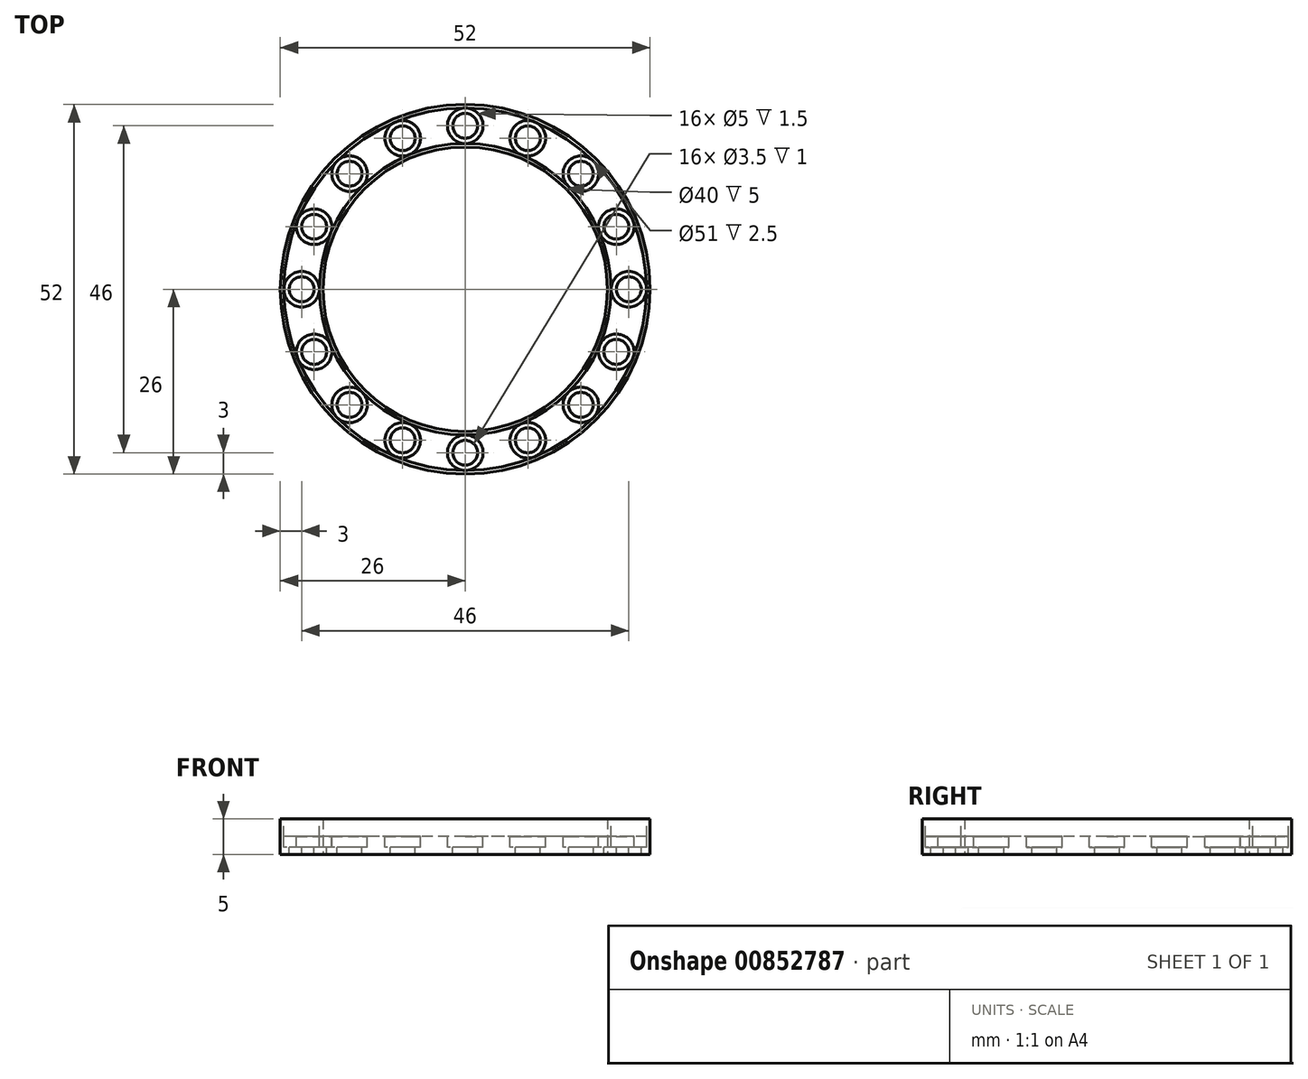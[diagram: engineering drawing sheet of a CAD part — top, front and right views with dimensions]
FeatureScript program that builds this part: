
annotation { "Feature Type Name" : "Feature", "Feature Type Description" : "" }
export const myFeature = defineFeature(function(context is Context, id is Id, definition is map)
    precondition{}
    {
        {
            var Q0;
            Q0=qCreatedBy(makeId("Top.planeOp"),FACE);
            var sketch = newSketch(context, id + "F0", { "sketchPlane" : qUnion([Q0])});
            skCircle(sketch, "E0", {"center": v(0, 0) * mm, "radius": 26 * mm});
            skCircle(sketch, "E1", {"center": v(0, 0) * mm, "radius": 20 * mm});
            skSolve(sketch);
        }
        {
            var Q0;
            Q0 = qSketchRegion(id + "F0", true);
            extrude(context, id + "F1", {"entities" : qUnion([Q0]), "depth" : 5 * mm, "offsetDistance" : 25 * mm});
        }
        {
            var Q0;
            Q0=makeQuery(id+"F1.opExtrude","CAP_FACE",FACE,{"disambiguationData":[OSD([sQuery(id+"F0.wireOp",EDGE,"E0"),sQuery(id+"F0.wireOp",EDGE,"E1")])],"isStart":false});
            var sketch = newSketch(context, id + "F2", { "sketchPlane" : qUnion([Q0])});
            skCircle(sketch, "E2", {"center": v(0, 0) * mm, "radius": 20.5 * mm});
            skCircle(sketch, "E3", {"center": v(0, 0) * mm, "radius": 25.5 * mm});
            skSolve(sketch);
        }
        {
            var Q0;
            Q0 = qSketchRegion(id + "F2", true);
            extrude(context, id + "F3", {"entities" : qUnion([Q0]), "operationType" : NewBodyOperationType.REMOVE, "oppositeDirection" : true, "depth" : 2.5 * mm, "offsetDistance" : 25 * mm});
        }
        {
            var Q0;
            Q0=makeQuery(id+"F3.boolean.opBoolean","COPY",FACE,{"derivedFrom":makeQuery(id+"F3.opExtrude","CAP_FACE",FACE,{"disambiguationData":[OSD([sQuery(id+"F2.wireOp",EDGE,"E2"),sQuery(id+"F2.wireOp",EDGE,"E3")])],"isStart":false})});
            var sketch = newSketch(context, id + "F4", { "sketchPlane" : qUnion([Q0])});
            skCircle(sketch, "E4", {"center": v(23, 0) * mm, "radius": 2.5 * mm});
            skCircle(sketch, "E5.1.0", {"center": v(21.25, -8.8) * mm, "radius": 2.5 * mm});
            skCircle(sketch, "E5.2.0", {"center": v(16.26, -16.26) * mm, "radius": 2.5 * mm});
            skCircle(sketch, "E5.3.0", {"center": v(8.8, -21.25) * mm, "radius": 2.5 * mm});
            skCircle(sketch, "E5.4.0", {"center": v(0, -23) * mm, "radius": 2.5 * mm});
            skCircle(sketch, "E5.5.0", {"center": v(-8.8, -21.25) * mm, "radius": 2.5 * mm});
            skCircle(sketch, "E5.6.0", {"center": v(-16.26, -16.26) * mm, "radius": 2.5 * mm});
            skCircle(sketch, "E5.7.0", {"center": v(-21.25, -8.8) * mm, "radius": 2.5 * mm});
            skCircle(sketch, "E5.8.0", {"center": v(-23, 0) * mm, "radius": 2.5 * mm});
            skCircle(sketch, "E5.9.0", {"center": v(-21.25, 8.8) * mm, "radius": 2.5 * mm});
            skCircle(sketch, "E5.10.0", {"center": v(-16.26, 16.26) * mm, "radius": 2.5 * mm});
            skCircle(sketch, "E5.11.0", {"center": v(-8.8, 21.25) * mm, "radius": 2.5 * mm});
            skCircle(sketch, "E5.12.0", {"center": v(0, 23) * mm, "radius": 2.5 * mm});
            skCircle(sketch, "E5.13.0", {"center": v(8.8, 21.25) * mm, "radius": 2.5 * mm});
            skCircle(sketch, "E5.14.0", {"center": v(16.26, 16.26) * mm, "radius": 2.5 * mm});
            skCircle(sketch, "E5.15.0", {"center": v(21.25, 8.8) * mm, "radius": 2.5 * mm});
            skPoint(sketch, "E5.center", {"position": v(0, 0) * mm});
            skLineSegment(sketch, "E5.anchor1", {"start": v(0, 0) * mm, "end": v(23, 0) * mm, "construction": true});
            skLineSegment(sketch, "E5.anchor2", {"start": v(0, 0) * mm, "end": v(21.25, 8.8) * mm, "construction": true});
            skSolve(sketch);
        }
        {
            var Q0;
            Q0 = qSketchRegion(id + "F4", true);
            extrude(context, id + "F5", {"entities" : qUnion([Q0]), "operationType" : NewBodyOperationType.REMOVE, "oppositeDirection" : true, "depth" : 1.5 * mm, "offsetDistance" : 25 * mm});
        }
        {
            var Q0;
            {var subQ0=sQuery(id+"F2.wireOp",EDGE,"E3");var subQ1=sQuery(id+"F2.wireOp",EDGE,"E2");var subQ2=makeQuery(id+"F3.boolean.opBoolean","COPY",FACE,{"derivedFrom":makeQuery(id+"F3.opExtrude","CAP_FACE",FACE,{"disambiguationData":[OSD([subQ1,subQ0])],"isStart":false})});Q0=makeQuery(id+"F5.boolean.opBoolean","SPLIT",FACE,{"disambiguationData":[TD([makeQuery(id+"F3.boolean.opBoolean","COPY",FACE,{"derivedFrom":makeQuery(id+"F3.opExtrude","SWEPT_FACE",FACE,{"disambiguationData":[OSD([subQ1])]})}),subQ2,makeQuery(id+"F3.boolean.opBoolean","COPY",FACE,{"derivedFrom":makeQuery(id+"F3.opExtrude","SWEPT_FACE",FACE,{"disambiguationData":[OSD([subQ0])]})}),makeQuery(id+"F5.opExtrude","SWEPT_FACE",FACE,{"disambiguationData":[OSD([sQuery(id+"F4.wireOp",EDGE,"E5.12.0")])]}),makeQuery(id+"F5.opExtrude","SWEPT_FACE",FACE,{"disambiguationData":[OSD([sQuery(id+"F4.wireOp",EDGE,"E5.13.0")])]})])],"derivedFrom":subQ2});}
            var sketch = newSketch(context, id + "F6", { "sketchPlane" : qUnion([Q0])});
            skCircle(sketch, "E6", {"center": v(23, 0) * mm, "radius": 1.75 * mm});
            skCircle(sketch, "E7.1.0", {"center": v(21.25, 8.8) * mm, "radius": 1.75 * mm});
            skCircle(sketch, "E7.2.0", {"center": v(16.26, 16.26) * mm, "radius": 1.75 * mm});
            skCircle(sketch, "E7.3.0", {"center": v(8.8, 21.25) * mm, "radius": 1.75 * mm});
            skCircle(sketch, "E7.4.0", {"center": v(0, 23) * mm, "radius": 1.75 * mm});
            skCircle(sketch, "E7.5.0", {"center": v(-8.8, 21.25) * mm, "radius": 1.75 * mm});
            skCircle(sketch, "E7.6.0", {"center": v(-16.26, 16.26) * mm, "radius": 1.75 * mm});
            skCircle(sketch, "E7.7.0", {"center": v(-21.25, 8.8) * mm, "radius": 1.75 * mm});
            skCircle(sketch, "E7.8.0", {"center": v(-23, 0) * mm, "radius": 1.75 * mm});
            skCircle(sketch, "E7.9.0", {"center": v(-21.25, -8.8) * mm, "radius": 1.75 * mm});
            skCircle(sketch, "E7.10.0", {"center": v(-16.26, -16.26) * mm, "radius": 1.75 * mm});
            skCircle(sketch, "E7.11.0", {"center": v(-8.8, -21.25) * mm, "radius": 1.75 * mm});
            skCircle(sketch, "E7.12.0", {"center": v(0, -23) * mm, "radius": 1.75 * mm});
            skCircle(sketch, "E7.13.0", {"center": v(8.8, -21.25) * mm, "radius": 1.75 * mm});
            skCircle(sketch, "E7.14.0", {"center": v(16.26, -16.26) * mm, "radius": 1.75 * mm});
            skCircle(sketch, "E7.15.0", {"center": v(21.25, -8.8) * mm, "radius": 1.75 * mm});
            skPoint(sketch, "E7.center", {"position": v(0, 0) * mm});
            skSolve(sketch);
        }
        {
            var Q0;
            Q0 = qSketchRegion(id + "F6", true);
            extrude(context, id + "F7", {"entities" : qUnion([Q0]), "operationType" : NewBodyOperationType.REMOVE, "endBound" : BoundingType.THROUGH_ALL, "oppositeDirection" : true, "depth" : 25 * mm, "offsetDistance" : 25 * mm});
        }
    });
